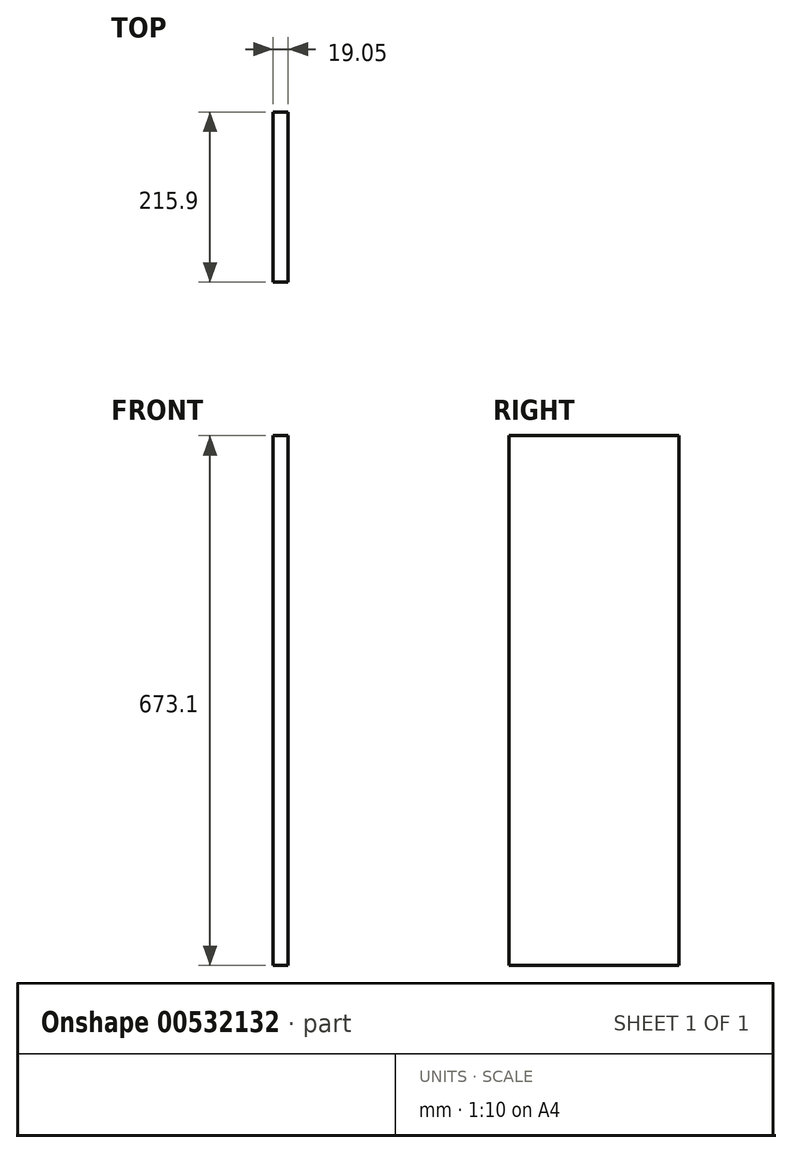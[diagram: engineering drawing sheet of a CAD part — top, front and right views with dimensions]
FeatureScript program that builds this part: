
annotation { "Feature Type Name" : "Feature", "Feature Type Description" : "" }
export const myFeature = defineFeature(function(context is Context, id is Id, definition is map)
    precondition{}
    {
        {
            var Q0;
            Q0=qCreatedBy(makeId("Right.planeOp"),FACE);
            var sketch = newSketch(context, id + "F0", { "sketchPlane" : qUnion([Q0])});
            skLineSegment(sketch, "E0.bottom", {"start": v(107.95, -336.55) * mm, "end": v(-107.95, -336.55) * mm});
            skLineSegment(sketch, "E0.top", {"start": v(107.95, 336.55) * mm, "end": v(-107.95, 336.55) * mm});
            skLineSegment(sketch, "E0.left", {"start": v(107.95, -336.55) * mm, "end": v(107.95, 336.55) * mm});
            skLineSegment(sketch, "E0.right", {"start": v(-107.95, -336.55) * mm, "end": v(-107.95, 336.55) * mm});
            skPoint(sketch, "E0.middle", {"position": v(0, 0) * mm});
            skSolve(sketch);
        }
        {
            var Q0;
            Q0 = qSketchRegion(id + "F0", true);
            extrude(context, id + "F1", {"entities" : qUnion([Q0]), "depth" : 19.05 * mm, "offsetDistance" : 25.4 * mm});
        }
    });
